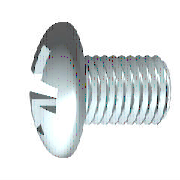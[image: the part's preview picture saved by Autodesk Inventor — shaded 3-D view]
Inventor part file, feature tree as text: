
AUTODESK INVENTOR PART (.ipt)
format: ipt  version: 2020 (Build 240168000, 168)  size: 278,528 bytes
history: native  units: mm (DEFAULTED — no unit token found)
features: other x2, plane x2, extrude x1
ambient origin geometry x7: Origin, YZ Plane, XZ Plane, X Axis, Y Axis, Z Axis, Center Point
bodies: Solid1 (feature_tree)
feature tree (5):
  other  "Базовый элемент"
  plane  "Work Plane1"
  extrude  "Паз"  Depth=4.0mm
  other  "Вырез"
  plane  "Work Plane3"
